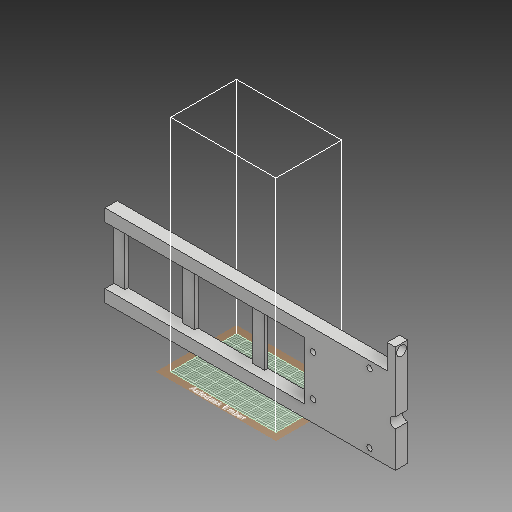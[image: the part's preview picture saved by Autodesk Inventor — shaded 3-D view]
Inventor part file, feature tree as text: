
AUTODESK INVENTOR PART (.ipt)
format: ipt  version: 2018 (Build 220112000, 112)  size: 879,616 bytes
history: native  units: mm
features: sketch x57, extrude x44, fillet x12, hole x8
ambient origin geometry x8: Origin, YZ Plane, XZ Plane, XY Plane, X Axis, Y Axis, Z Axis, Center Point
bodies: Solid1 (feature_tree)
feature tree (121):
  extrude  "Extrusion1"  Depth=50.0mm
  hole  "Hole1"  [1 undecoded]
  hole  "Hole2"  [1 undecoded]
  extrude  "Extrusion2"  Depth=25.0mm
  extrude  "Extrusion3"  Depth=25.0mm
  extrude  "Extrusion4"  Depth=5.0mm
  sketch  "Sketch7"  dims[d25=10.0mm d26=5.0mm]
  extrude  "Extrusion5"  Depth=5.0mm
  extrude  "Extrusion6"  Depth=35.0mm
  extrude  "Extrusion7"  Depth=35.0mm
  extrude  "Extrusion8"  Depth=35.0mm
  extrude  "Extrusion9"  Depth=2.0mm TaperAngle=0.0deg
  extrude  "Extrusion10"  Depth=7.5mm TaperAngle=0.0deg
  extrude  "Extrusion11"  Depth=10.0mm
  extrude  "Extrusion12"  Depth=7.5mm
  fillet  "Fillet1"  Radius=7.5mm
  fillet  "Fillet2"  Radius=25.0mm
  fillet  "Fillet3"  Radius=3.0mm
  fillet  "Fillet4"  Radius=3.2mm
  fillet  "Fillet5"  Radius=2.1mm
  fillet  "Fillet6"  Radius=5.5mm
  extrude  "Extrusion13"  Depth=92.5mm TaperAngle=0.0deg
  sketch  "Sketch17"  dims[d58=4.25mm d59=241.0mm d60=0.0mm]
  hole  "Hole3"  [1 undecoded]
  hole  "Hole4"  [1 undecoded]
  extrude  "Extrusion14"  Depth=5.0mm
  extrude  "Extrusion15"  Depth=2.5mm TaperAngle=0.0deg
  extrude  "Extrusion16"  Depth=6.35mm
  extrude  "Extrusion17"  Depth=2.5mm
  extrude  "Extrusion18"  Depth=14.55mm TaperAngle=0.0deg
  extrude  "Extrusion19"  Depth=0.1mm
  extrude  "Extrusion20"  Depth=3.25mm
  extrude  "Extrusion21"  Depth=3.25mm
  hole  "Hole5"  [1 undecoded]
  extrude  "Extrusion22"  Depth=2.0mm
  extrude  "Extrusion23"  Depth=15.0mm
  extrude  "Extrusion24"  Depth=10.0mm TaperAngle=0.0deg
  hole  "Hole6"  [1 undecoded]
  extrude  "Extrusion25"  Depth=100.0mm TaperAngle=0.0deg
  extrude  "Extrusion26"  Depth=2.0mm TaperAngle=0.0deg
  extrude  "Extrusion27"  Depth=3.3mm
  extrude  "Extrusion28"  Depth=3.3mm
  hole  "Hole7"  [1 undecoded]
  extrude  "Extrusion29"  Depth=2.0mm
  extrude  "Extrusion30"  Depth=17.0mm
  hole  "Hole8"  [1 undecoded]
  extrude  "Extrusion31"  Depth=21.0mm
  extrude  "Extrusion32"  Depth=10.0mm
  fillet  "Fillet7"  Radius=3.3mm
  fillet  "Fillet8"  Radius=10.0mm
  extrude  "Extrusion33"  Depth=5.0mm
  extrude  "Extrusion34"  Depth=5.0mm
  sketch  "Sketch45"  dims[d149=10.0mm d150=17.5mm d151=0.0mm]
  sketch  "Sketch46"  dims[d152=5.0mm]
  extrude  "Extrusion35"  Depth=10.0mm TaperAngle=0.0deg
  extrude  "Extrusion36"  Depth=2.0mm TaperAngle=0.0deg
  extrude  "Extrusion37"  Depth=3.75mm
  extrude  "Extrusion38"  Depth=3.75mm
  extrude  "Extrusion39"  Depth=10.0mm TaperAngle=0.0deg
  extrude  "Extrusion40"  Depth=2.0mm TaperAngle=0.0deg
  fillet  "Fillet9"  Radius=5.0mm
  fillet  "Fillet10"  Radius=15.0mm
  fillet  "Fillet11"  Radius=7.5mm
  fillet  "Fillet12"  Radius=17.5mm
  extrude  "Extrusion41"  Depth=47.5mm
  extrude  "Extrusion42"  Depth=5.0mm
  sketch  "Sketch55"  dims[d200=20.0mm d203=5.0mm]
  extrude  "Extrusion43"  Depth=29.0mm
  extrude  "Extrusion44"  Depth=7.5mm TaperAngle=0.0deg
  sketch  "Sketch1"  dims[d0=50.0mm d1=50.0mm]
  sketch  "Sketch2"  dims[d2=240.0mm d3=7.5mm]
  sketch  "Sketch3"  dims[d4=7.5mm d5=7.5mm d6=0.0mm]
  sketch  "Sketch4"  dims[d7=6.35mm d8=6.0mm d9=4.0mm d10=2.0mm d11=90.0deg d12=8.0mm d13=20.594885mm d14=25.0mm]
  sketch  "Sketch5"  dims[d15=3.3mm d16=6.0mm d17=4.0mm d18=2.0mm d19=90.0deg d20=8.0mm d21=20.594885mm d22=25.0mm]
  sketch  "Sketch6"  dims[d23=180.0deg d24=5.0mm]
  sketch  "Sketch8"  dims[d27=17.5mm d28=0.0mm d30=35.0mm]
  sketch  "Sketch9"  dims[d31=35.0mm d32=35.0mm]
  sketch  "Sketch10"  dims[d33=35.0mm d34=35.0mm]
  sketch  "Sketch11"  dims[d35=35.0mm d36=2.0mm d37=0.0mm]
  sketch  "Sketch12"  dims[d38=10.0mm d39=7.5mm d40=0.0mm]
  sketch  "Sketch13"  dims[d41=100.0mm d42=10.0mm]
  sketch  "Sketch14"  dims[d43=7.5mm d44=0.0mm d45=7.5mm d46=7.5mm d47=25.0mm d48=0.0mm d49=3.0mm d50=3.2mm d51=2.1mm d52=5.5mm]
  sketch  "Sketch15"  dims[d53=3.3mm d54=92.5mm d55=0.0mm]
  sketch  "Sketch16"  dims[d56=5.5mm d57=3.3mm]
  sketch  "Sketch18"  dims[d61=4.44mm d62=5.0mm]
  sketch  "Sketch19"  dims[d63=2.5mm d64=91.25mm d65=0.0mm]
  sketch  "Sketch20"  dims[d66=30.0mm d67=6.35mm]
  sketch  "Sketch21"  dims[d68=3.8mm d69=0.0mm d70=2.5mm]
  sketch  "Sketch22"  dims[d71=14.55mm d72=0.0mm d73=14.55mm d74=0.0mm]
  sketch  "Sketch23"  dims[d75=0.1mm d76=0.1mm]
  sketch  "Sketch24"  dims[d77=3.25mm d78=3.25mm]
  sketch  "Sketch25"  dims[d79=3.25mm d80=3.25mm]
  sketch  "Sketch26"  dims[d81=35.0mm d82=10.0mm]
  sketch  "Sketch27"  dims[d83=2.0mm d84=0.0mm d85=3.6mm]
  sketch  "Sketch28"  dims[d86=3.6mm]
  sketch  "Sketch29"  dims[d87=3.3mm d88=6.0mm d89=4.0mm d90=2.0mm d91=90.0deg d92=15.0mm d93=20.594885mm]
  sketch  "Sketch30"  dims[d94=3.3mm d95=6.0mm d96=4.0mm d97=2.0mm d98=90.0deg d99=15.0mm d100=20.594885mm d101=6.0mm]
  sketch  "Sketch31"  dims[d102=20.0mm d103=0.0mm d104=10.0mm d105=0.0mm]
  sketch  "Sketch32"  dims[d106=2.0mm d107=0.0mm d108=4.0mm]
  sketch  "Sketch33"  dims[d109=100.0mm d110=0.0mm d111=100.0mm d112=0.0mm]
  sketch  "Sketch34"  dims[d113=5.0mm d114=2.0mm d115=0.0mm]
  sketch  "Sketch35"  dims[d116=3.3mm d117=3.3mm]
  sketch  "Sketch36"  dims[d118=3.3mm d119=3.3mm]
  sketch  "Sketch37"  dims[d120=2.0mm d121=0.0mm d122=5.5mm d123=0.0mm]
  sketch  "Sketch38"  dims[d124=3.3mm d125=6.0mm d126=4.0mm d127=2.0mm d128=90.0deg d129=8.0mm d130=20.594885mm d131=42.0mm]
  sketch  "Sketch39"  dims[d132=17.0mm d133=21.0mm]
  sketch  "Sketch40"  dims[d135=8.5mm d136=15.825mm]
  sketch  "Sketch41"  dims[d137=3.5mm d138=21.0mm]
  sketch  "Sketch42"  dims[d139=3.3mm d140=3.3mm d141=3.3mm d142=10.0mm d143=0.0mm]
  sketch  "Sketch43"  dims[d144=7.5mm d145=0.0mm d146=5.0mm]
  sketch  "Sketch44"  dims[d147=10.0mm d148=5.0mm]
  sketch  "Sketch47"  dims[d153=7.0mm d154=6.0mm d155=4.0mm d156=2.0mm d157=90.0deg d158=8.0mm d159=20.594885mm d160=17.5mm d161=0.0mm]
  sketch  "Sketch48"  dims[d162=170.5mm d163=0.0mm d164=3.75mm]
  sketch  "Sketch49"  dims[d165=3.75mm d166=3.75mm]
  sketch  "Sketch50"  dims[d167=3.75mm d168=10.0mm d169=0.0mm]
  sketch  "Sketch51"  dims[d170=100.0mm d171=0.0mm]
  sketch  "Sketch52"  dims[d172=5.0mm d173=6.0mm d174=4.0mm d175=2.0mm d176=90.0deg d177=15.0mm d178=0.0mm d179=2.0mm d180=0.0mm d181=5.0mm d182=15.0mm d183=0.0mm d184=7.5mm]
  sketch  "Sketch53"  dims[d185=6.0mm d186=6.0mm d187=4.0mm d188=2.0mm d189=90.0deg d190=15.0mm d191=0.0mm d192=17.5mm d193=0.0mm]
  sketch  "Sketch54"  dims[d194=23.75mm d195=47.5mm]
  sketch  "Sketch56"  dims[d204=5.0mm d205=29.0mm]
  sketch  "Sketch57"  dims[d206=29.0mm d207=7.5mm d208=0.0mm d209=4.0mm d210=4.0mm d211=2.0mm d212=0.0mm d213=12.0mm d214=2.0mm d215=0.0mm d216=7.5mm d217=7.5mm d218=20.0mm d219=0.0mm d220=20.0mm d221=3.3mm d222=20.0mm d223=0.0mm d224=4.0mm d225=4.0mm d226=10.0mm d227=0.0mm d228=3.0mm d229=5.5mm d230=0.0mm d231=10.0mm d232=0.0mm d233=74.724mm d234=74.724mm d235=85.515mm d236=5.0mm d237=5.0mm d238=85.515mm d239=5.0mm d240=85.515mm d241=5.0mm d242=2.0mm d243=0.0mm d244=2.0mm d245=2.0mm d246=2.0mm d247=2.0mm d248=10.0mm d249=2.0mm d250=0.0mm d251=1.0mm d252=0.0mm d253=20.0mm d254=1.0mm d255=0.0mm d256=0.5mm d257=0.0mm]
note: 8 required parameter values undecoded (feature->parameter linkage not recoverable at this tier; creation-order binding heuristic only, values carry confidence <= 0.55)
